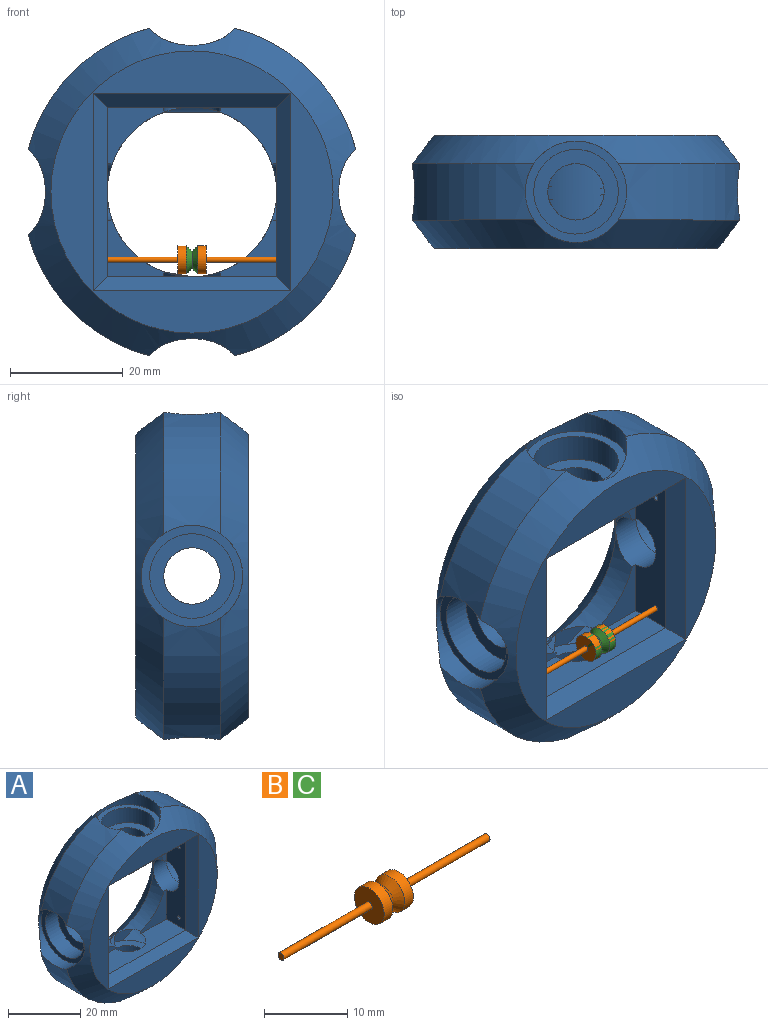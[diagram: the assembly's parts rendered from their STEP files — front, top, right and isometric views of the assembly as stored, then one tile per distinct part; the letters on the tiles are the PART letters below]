
ASSEMBLY  parts=3 mates=1
PART A: 55 faces, bbox 80x40x80 mm
  f0: cylinder r=15mm len=15mm, axis (0,1,0), area 78mm2, adj f1,f2,f3,f4
  f1: plane 10x10mm, normal (0,-1,0), area 45.5mm2, adj f0,f2,f4,f5,f6
  f2: cylinder r=5mm len=10mm, axis (1,0,0), area 163.8mm2, adj f0,f1,f5,f7,f8,f9
  f3: cone r=20mm half-angle=45deg, axis (0,1,0), area 777.5mm2, adj f0,f9,f10,f11,f12
  f4: cylinder r=5mm len=10mm, axis (0,0,-1), area 6.7mm2, adj f0,f1,f6,f11,f13
  f5: plane 30x7.5mm, normal (1,0,0), area 184.2mm2, adj f1,f2,f6,f8,f14,f15,f16,f17
  f6: plane 30x7.5mm, normal (0,0,1), area 185.7mm2, adj f1,f4,f5,f13,f18,f19
  f7: plane 15x15mm, normal (-1,0,0), area 98.2mm2, adj f2,f20
  f8: plane 10x10mm, normal (0,-1,0), area 45.5mm2, adj f2,f5,f9,f16,f21
  f9: cylinder r=15mm len=15mm, axis (0,1,0), area 78mm2, adj f2,f3,f8,f21
  f10: cylinder r=15mm len=15mm, axis (0,1,0), area 78mm2, adj f3,f21,f22,f23,f24
  f11: cylinder r=15mm len=15mm, axis (0,1,0), area 78mm2, adj f3,f4,f13,f23
  f12: plane 50x50mm, normal (0,1,0), area 706.9mm2, adj f3,f25
  f13: plane 10x10mm, normal (0,-1,0), area 45.5mm2, adj f4,f6,f11,f19,f23
  f14: cylinder r=0.5mm len=2.5mm, axis (-1,0,0), area 7.9mm2, adj f5,f26
  f15: cylinder r=0.5mm len=2.5mm, axis (-1,0,0), area 7.9mm2, adj f5,f27
  f16: plane 30x7.5mm, normal (0,0,-1), area 185.7mm2, adj f5,f8,f19,f21,f22,f28
  f17: plane 35x2.5mm, normal (0.71,-0.71,0), area 114.9mm2, adj f5,f18,f28,f29
  f18: plane 35x2.5mm, normal (0,-0.71,0.71), area 114.9mm2, adj f6,f17,f29,f30
  f19: plane 30x7.5mm, normal (-1,0,0), area 184.2mm2, adj f6,f13,f16,f22,f23,f30,f31,f32
  f20: cylinder r=7.5mm len=15mm, axis (-1,0,0), area 235.6mm2, adj f7,f33
  f21: cylinder r=5mm len=10mm, axis (0,0,-1), area 163.8mm2, adj f8,f9,f10,f16,f22,f34
  f22: plane 10x10mm, normal (0,-1,0), area 45.5mm2, adj f10,f16,f19,f21,f23
  f23: cylinder r=5mm len=10mm, axis (1,0,0), area 163.8mm2, adj f10,f11,f13,f19,f22,f35
  f24: cylinder r=5mm len=0mm, axis (0,0,-1), area 0mm2, adj f10
  f25: cone r=30mm half-angle=45deg, axis (0,-1,0), area 981.8mm2, adj f12,f36,f37,f38,f39,f40,f41,f42
  f26: plane 1x1mm, normal (1,0,0), area 0.8mm2, adj f14
  f27: plane 1x1mm, normal (1,0,0), area 0.8mm2, adj f15
  f28: plane 35x2.5mm, normal (0,-0.71,-0.71), area 114.9mm2, adj f16,f17,f29,f30
  f29: plane 50x50mm, normal (0,-1,0), area 738.5mm2, adj f17,f18,f28,f30,f44
  f30: plane 35x2.5mm, normal (-0.71,-0.71,0), area 114.9mm2, adj f18,f19,f28,f29
  f31: cylinder r=0.5mm len=2.5mm, axis (-1,0,0), area 7.9mm2, adj f19,f45
  f32: cylinder r=0.5mm len=2.5mm, axis (-1,0,0), area 7.9mm2, adj f19,f46
  f33: plane 18x18mm, normal (-1,0,0), area 77.8mm2, adj f20,f38
  f34: plane 15x15mm, normal (0,0,1), area 98.2mm2, adj f21,f47
  f35: plane 15x15mm, normal (1,0,0), area 98.2mm2, adj f23,f48
  f36: cylinder r=9mm len=18mm, axis (0,0,-1), area 150.5mm2, adj f25,f37,f43,f44,f49
  f37: cylinder r=30mm len=21.57mm, axis (0,1,0), area 298.6mm2, adj f25,f36,f38,f44
  f38: cylinder r=9mm len=18mm, axis (-1,0,0), area 150.4mm2, adj f25,f33,f37,f39,f44
  f39: cylinder r=30mm len=21.57mm, axis (0,1,0), area 298.6mm2, adj f25,f38,f40,f44
  f40: cylinder r=9mm len=18mm, axis (0,0,1), area 150.4mm2, adj f25,f39,f41,f44,f50
  f41: cylinder r=30mm len=21.57mm, axis (0,1,0), area 298.6mm2, adj f25,f40,f42,f44
  f42: cylinder r=9mm len=18mm, axis (1,0,0), area 150.4mm2, adj f25,f41,f43,f44,f51
  f43: cylinder r=30mm len=21.57mm, axis (0,1,0), area 298.6mm2, adj f25,f36,f42,f44
  f44: cone r=25mm half-angle=45deg, axis (0,1,0), area 981.7mm2, adj f29,f36,f37,f38,f39,f40,f41,f42
  f45: plane 1x1mm, normal (-1,0,0), area 0.8mm2, adj f31
  f46: plane 1x1mm, normal (-1,0,0), area 0.8mm2, adj f32
  f47: cylinder r=7.5mm len=15mm, axis (0,0,1), area 235.6mm2, adj f34,f50
  f48: cylinder r=7.5mm len=15mm, axis (1,0,0), area 235.6mm2, adj f35,f51
  f49: plane 18x18mm, normal (0,0,-1), area 77.8mm2, adj f36,f52
  f50: plane 18x18mm, normal (0,0,1), area 77.8mm2, adj f40,f47
  f51: plane 18x18mm, normal (1,0,0), area 77.8mm2, adj f42,f48
  f52: cylinder r=7.5mm len=15mm, axis (0,0,-1), area 235.6mm2, adj f49,f53
  f53: plane 35x35mm, normal (0,0,-1), area 98.2mm2, adj f52,f54
  f54: cylinder r=5mm len=10mm, axis (0,0,-1), area 0mm2, adj f53
PART B: 11 faces, bbox 35x5x5 mm
  f0: cylinder r=0.5mm len=15mm, axis (-1,0,0), area 47.1mm2, adj f1,f3
  f1: plane 1x1mm, normal (1,0,0), area 0.8mm2, adj f0
  f2: cylinder r=2.5mm len=5mm, axis (-1,0,0), area 23.6mm2, adj f3,f4
  f3: plane 5x5mm, normal (1,0,0), area 18.8mm2, adj f0,f2
  f4: cone r=2.5mm half-angle=45deg, axis (1,0,0), area 17.8mm2, adj f2,f7
  f5: cylinder r=2.52mm len=5.05mm, axis (1,0,0), area 23.8mm2, adj f6,f10
  f6: plane 5.05x5.05mm, normal (-1,0,0), area 19.2mm2, adj f5,f9
  f7: plane 3.05x3.05mm, normal (1,0,0), area 0.2mm2, adj f4,f10
  f8: plane 1x1mm, normal (-1,0,0), area 0.8mm2, adj f9
  f9: cylinder r=0.5mm len=15mm, axis (-1,0,0), area 47.1mm2, adj f6,f8
  f10: cone r=1.52mm half-angle=45deg, axis (-1,0,0), area 18mm2, adj f5,f7
PART C: same geometry as B
PLACE A t=(0,5,12)mm
PLACE B at identity
PLACE C at identity
MATE revolute A.f15 <-> C.f0  axis (-1,0,0) through (-17.5,0,0)mm
